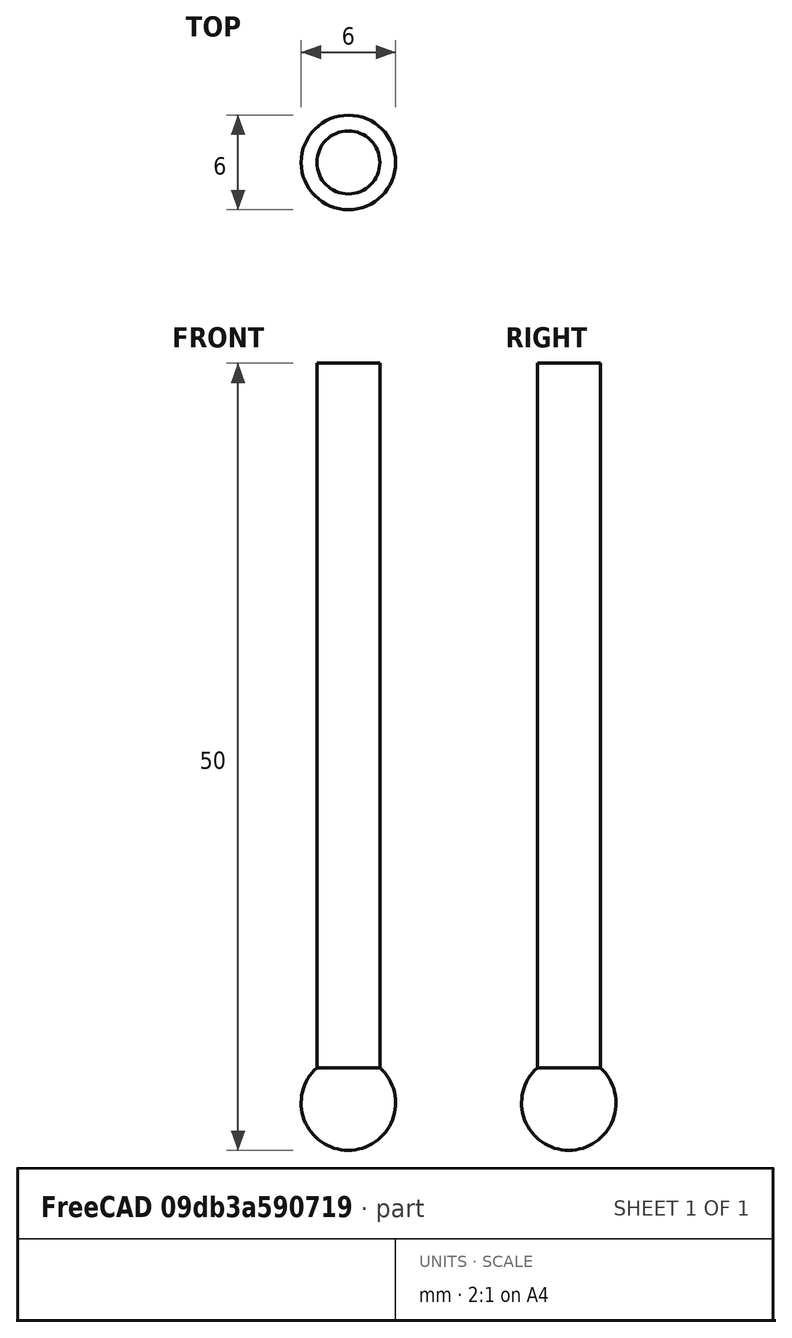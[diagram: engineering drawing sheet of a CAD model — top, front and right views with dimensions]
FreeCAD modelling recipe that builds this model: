
FCSTD DOCUMENT  (FreeCAD 1.0R39109 (Git))
Label: probe
License: Creative Commons Attribution 4.0
LicenseURL: https://creativecommons.org/licenses/by/4.0/
objects: Sketcher::SketchObject×1, PartDesign::Revolution×1, App::FeaturePython×1, PartDesign::Body×1
note: 6 computed .brp shape members not serialized (recipe doc carries the construction recipe); baked Part::Feature solids carry a one-line shape summary decoded from their .brp

FEATURE [Sketcher::SketchObject] Sketch
  ArcFitTolerance = 0
  AttachmentSupport = -> [XZ_Plane]
  FullyConstrained = true
  MakeInternals = false
  MapMode = 5
  Placement = pos=(0,0,0) rot=(1,0,0;1.5708rad)
  expr: Constraints[11] = <<Attributes>>.Diameter
  expr: Constraints[15] = <<Attributes>>.Length
  expr: Constraints[8] = <<Attributes>>.ShaftDiameter
  sketch-geometry (6):
    g0: LineSegment StartX=-6e-16 StartY=0 StartZ=0 EndX=2 EndY=0 EndZ=0
    g1: LineSegment StartX=2 StartY=0 StartZ=0 EndX=2 EndY=-44.7639 EndZ=0
    g2: LineSegment StartX=-6e-16 StartY=-50 StartZ=0 EndX=-6e-16 EndY=0 EndZ=0
    g3: LineSegment [constr] StartX=-2 StartY=0 StartZ=0 EndX=2 EndY=0 EndZ=0
    g4: ArcOfCircle CenterX=0 CenterY=-47 CenterZ=0 NormalX=0 NormalY=0 NormalZ=1 AngleXU=0 Radius=3 StartAngle=4.71239 EndAngle=7.12425
    g5: LineSegment [constr] StartX=0 StartY=-47 StartZ=0 EndX=0 EndY=-53 EndZ=0
  constraints (16):
    c: Coincident(g0,g1)
    c: Coincident(g2,g0)
    c: Horizontal(g0)
    c: Vertical(g1)
    c: Vertical(g2)
    c: Coincident(g0,g-1)
    c: Symmetric(g3,g3,g-2)
    c: Coincident(g0,g3)
    c: DistanceX(g3,g3) = 4
    c: PointOnObject(g4,g2)
    c: Coincident(g4,g2)
    c: DistanceY(g5,g5) = 6
    c: Coincident(g5,g4)
    c: Coincident(g4,g1)
    c: Symmetric(g4,g5,g2)
    c: DistanceY(g2,g2) = 50
FEATURE [PartDesign::Revolution] Revolution
  AllowMultiFace = false
  Angle = 360
  Angle2 = 60
  Axis = (0,2e-16,1)
  Base = (0,0,0)
  Placement = pos=(0,0,0) rot=(1,0,0;1.5708rad)
  Profile = -> Sketch
  ReferenceAxis = -> Sketch [V_Axis]
  Reversed = true
  Suppressed = false
  Type = 0
FEATURE [App::FeaturePython] PropertyBag  label="Attributes"  # WARN: FeaturePython — macro-defined, semantics opaque (R4)
  CustomPropertyGroups = 0
  Diameter = 6
  Length = 50
  ShaftDiameter = 4
FEATURE [PartDesign::Body] Body  label="Probe"
  AllowCompound = false
  Group = -> [Sketch,Revolution,PropertyBag]
  Origin = -> Origin
  Tip = -> Revolution
